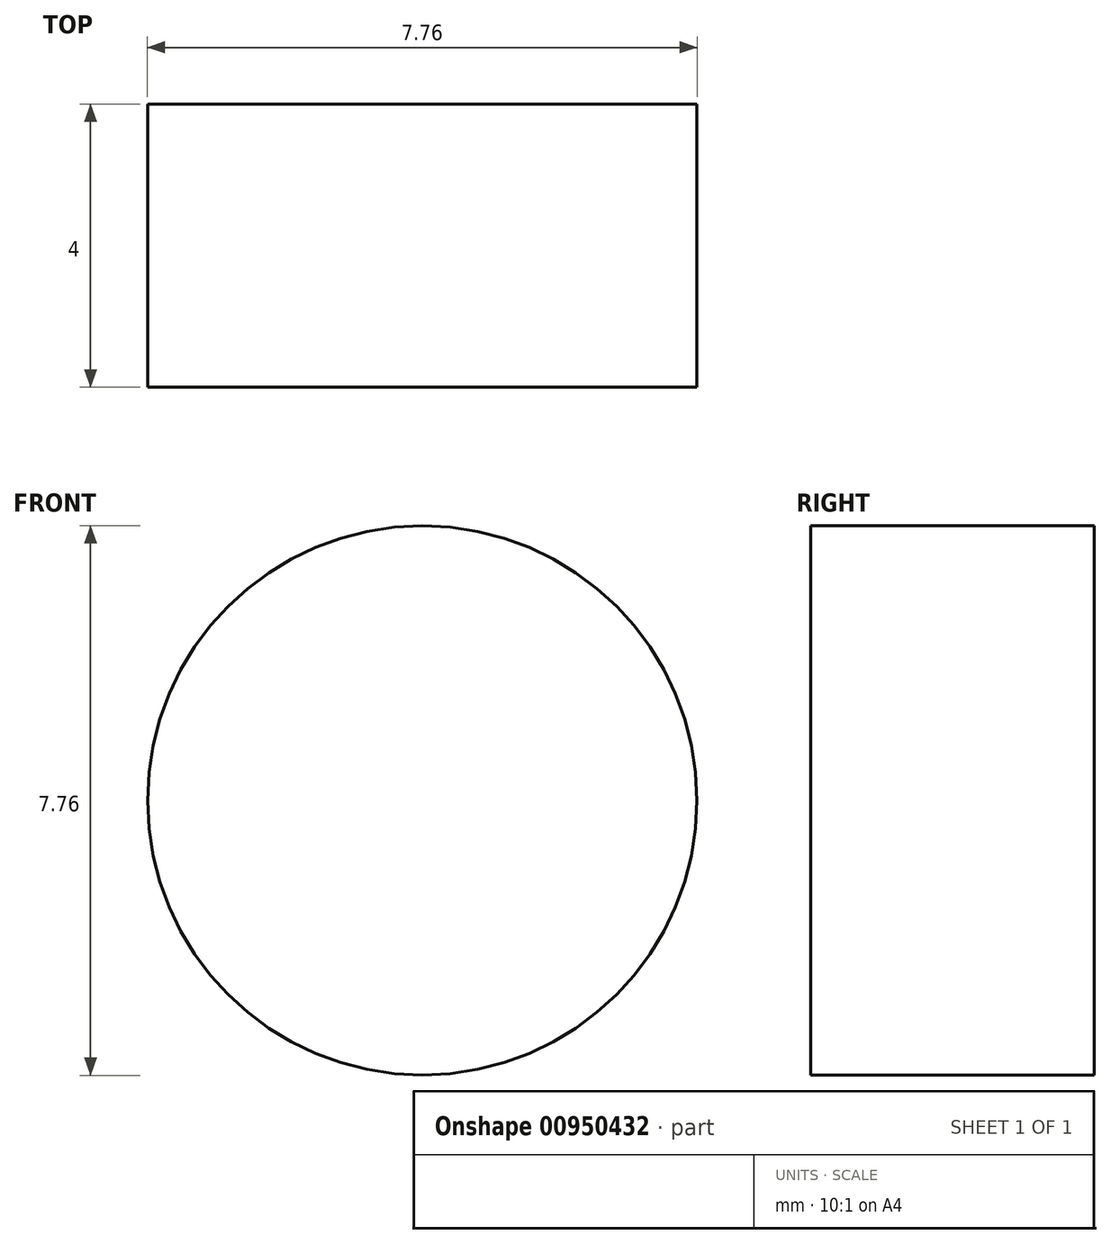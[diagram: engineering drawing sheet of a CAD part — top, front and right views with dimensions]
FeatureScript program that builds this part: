
annotation { "Feature Type Name" : "Feature", "Feature Type Description" : "" }
export const myFeature = defineFeature(function(context is Context, id is Id, definition is map)
    precondition{}
    {
        {
            var Q0;
            Q0=qCreatedBy(makeId("Front.planeOp"),FACE);
            var sketch = newSketch(context, id + "F0", { "sketchPlane" : qUnion([Q0])});
            skCircle(sketch, "E0", {"center": v(0, 0) * mm, "radius": 3.88 * mm});
            skSolve(sketch);
        }
        {
            var Q0;
            Q0=makeQuery(id+"F0.imprint","IMPRINT",FACE,{"disambiguationData":[TD([[makeQuery(id+"F0.imprint","IMPRINT",EDGE,{"derivedFrom":sQuery(id+"F0.wireOp",EDGE,"E0")}),1.0]])]});
            extrude(context, id + "F1", {"entities" : qUnion([Q0]), "depth" : 4 * mm, "offsetDistance" : 25 * mm});
        }
    });
